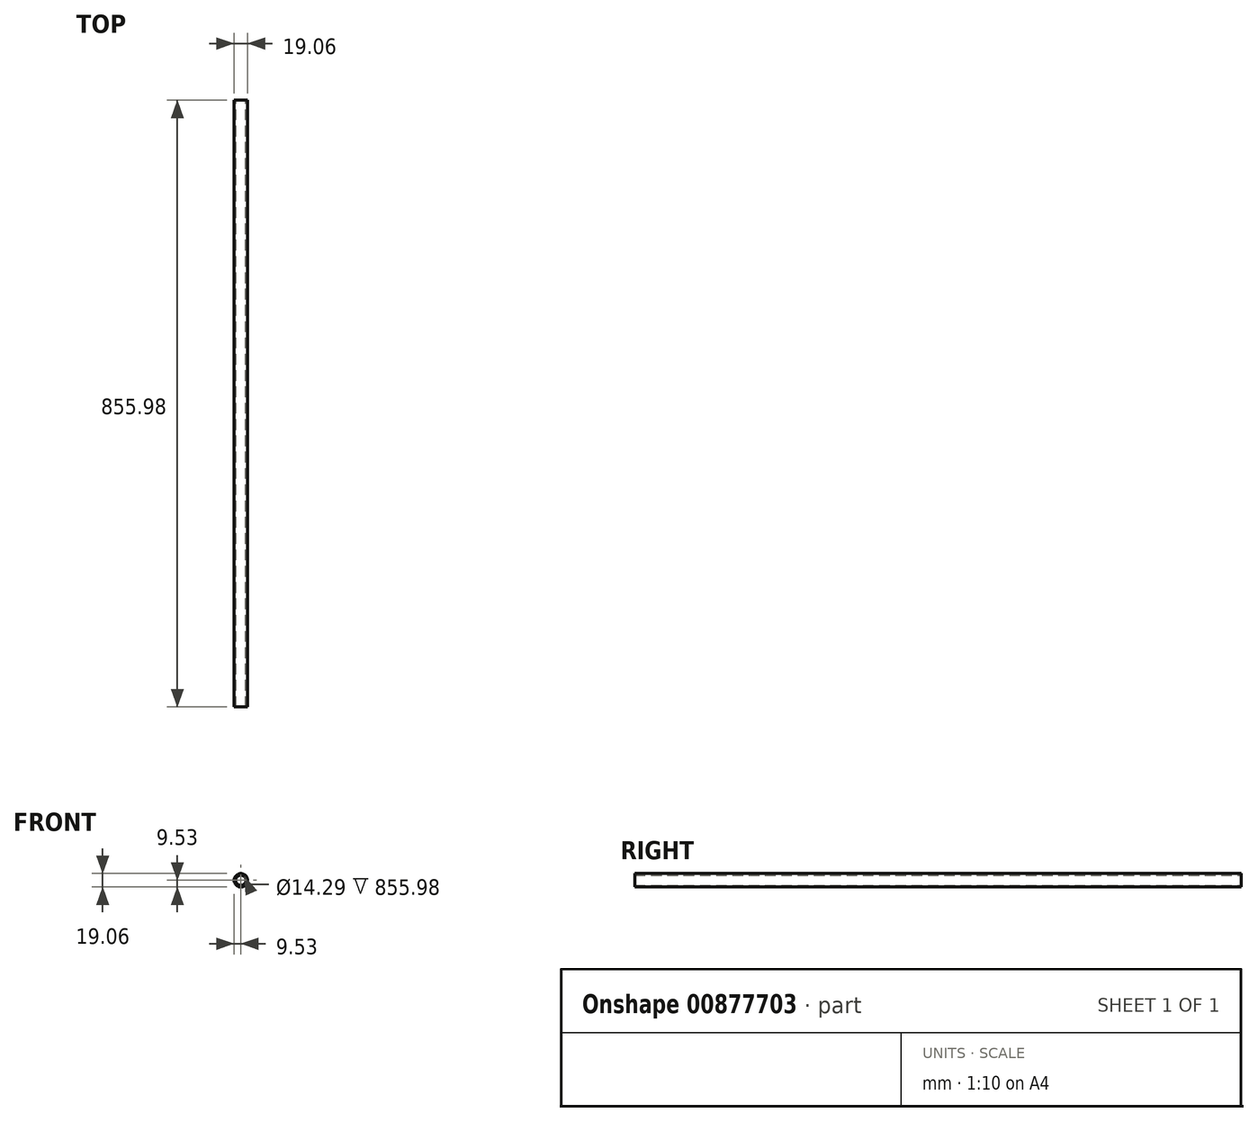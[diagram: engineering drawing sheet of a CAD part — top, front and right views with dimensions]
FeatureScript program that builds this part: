
annotation { "Feature Type Name" : "Feature", "Feature Type Description" : "" }
export const myFeature = defineFeature(function(context is Context, id is Id, definition is map)
    precondition{}
    {
        {
            var Q0;
            Q0=qCreatedBy(makeId("Front.planeOp"),FACE);
            var sketch = newSketch(context, id + "F0", { "sketchPlane" : qUnion([Q0])});
            skCircle(sketch, "E0", {"center": v(0, 0) * mm, "radius": 7.14 * mm});
            skCircle(sketch, "E1", {"center": v(0, 0) * mm, "radius": 9.53 * mm});
            skSolve(sketch);
        }
        {
            var Q0;
            Q0=makeQuery(id+"F0.imprint","IMPRINT",FACE,{"disambiguationData":[TD([[makeQuery(id+"F0.imprint","IMPRINT",EDGE,{"derivedFrom":sQuery(id+"F0.wireOp",EDGE,"E0")}),-1.0]])]});
            extrude(context, id + "F1", {"entities" : qUnion([Q0]), "depth" : 754.38 * mm, "offsetDistance" : 25.4 * mm, "hasSecondDirection" : true, "secondDirectionOppositeDirection" : true, "secondDirectionDepth" : 101.6 * mm});
        }
    });
